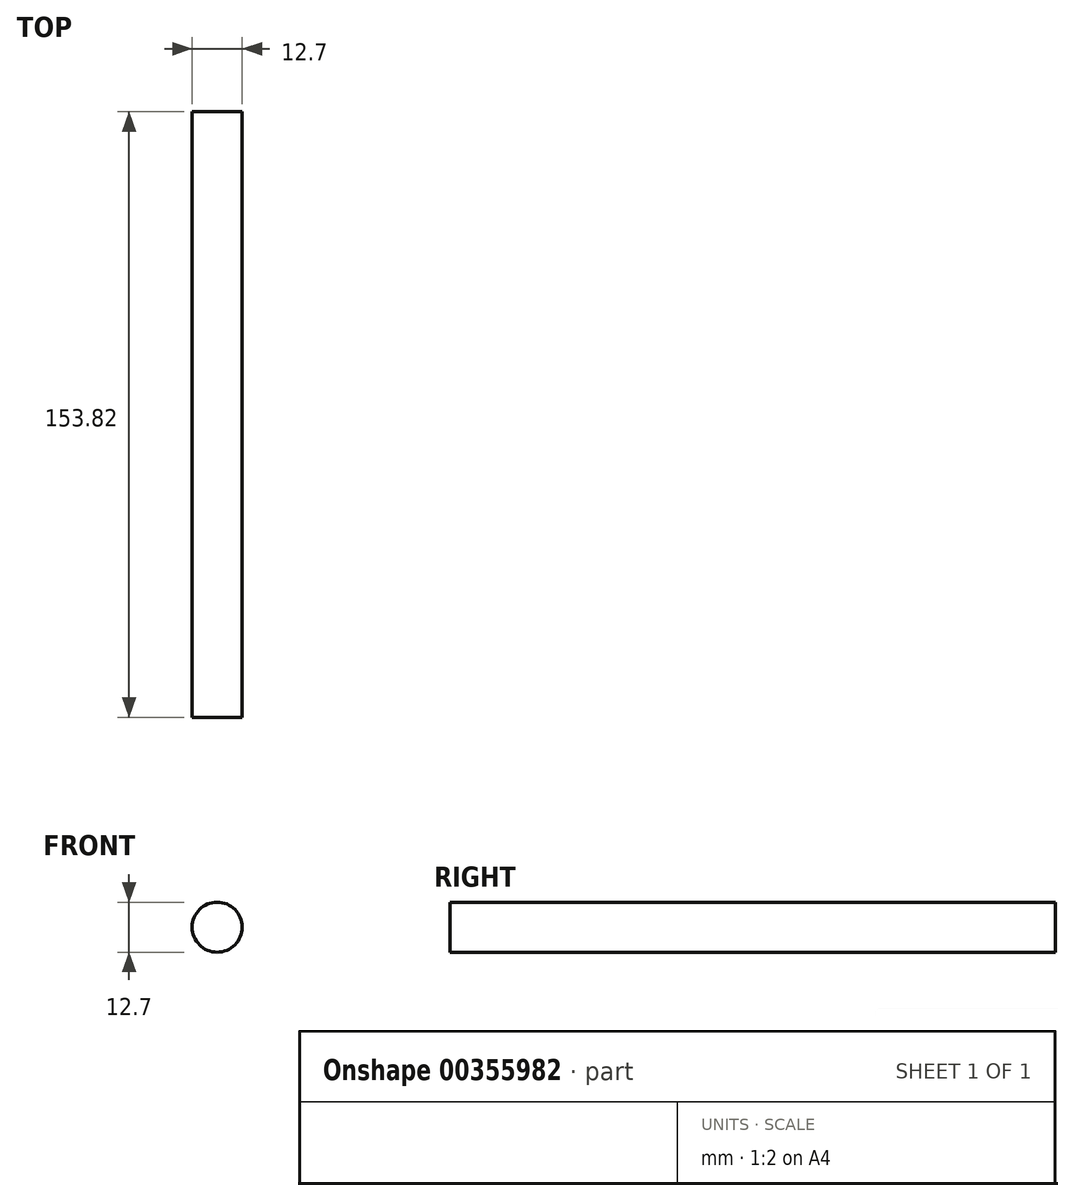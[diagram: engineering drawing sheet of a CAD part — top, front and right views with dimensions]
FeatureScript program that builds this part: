
annotation { "Feature Type Name" : "Feature", "Feature Type Description" : "" }
export const myFeature = defineFeature(function(context is Context, id is Id, definition is map)
    precondition{}
    {
        {
            var Q0;
            Q0=qCreatedBy(makeId("Front.planeOp"),FACE);
            var sketch = newSketch(context, id + "F0", { "sketchPlane" : qUnion([Q0])});
            skCircle(sketch, "E0", {"center": v(0, 0) * mm, "radius": 6.35 * mm});
            skSolve(sketch);
        }
        {
            var Q0;
            Q0=qSketchRegion(id+"F0",true);
            extrude(context, id + "F1", {"entities" : qUnion([Q0]), "depth" : 153.82 * mm});
        }
    });
